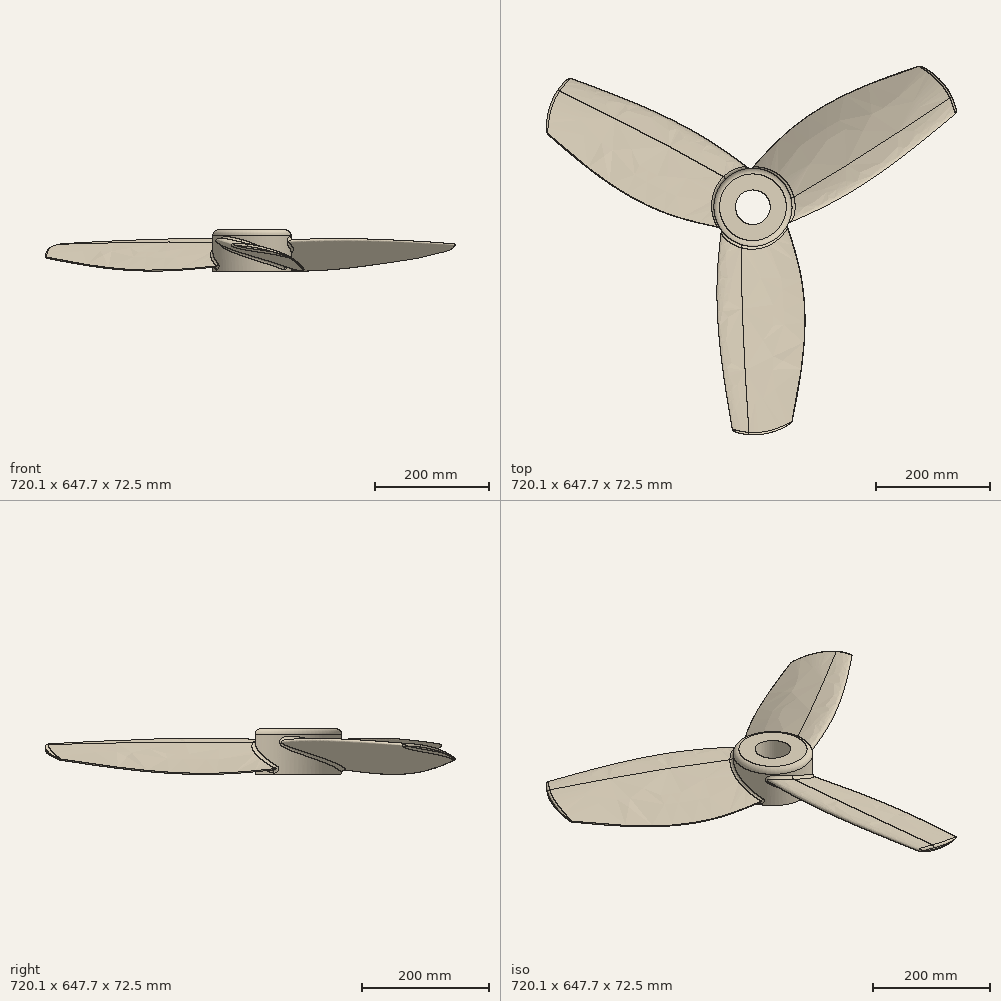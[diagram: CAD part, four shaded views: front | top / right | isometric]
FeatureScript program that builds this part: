
annotation { "Feature Type Name" : "Feature", "Feature Type Description" : "" }
export const myFeature = defineFeature(function(context is Context, id is Id, definition is map)
    precondition{}
    {
        {
            var Q0;
            Q0=qCreatedBy(makeId("Front.planeOp"),FACE);
            var sketch = newSketch(context, id + "F0", { "sketchPlane" : qUnion([Q0])});
            skLineSegment(sketch, "E0", {"start": v(-25.68, 10.16) * mm, "end": v(0, 0) * mm, "construction": true});
            skLineSegment(sketch, "E1", {"start": v(0, 0) * mm, "end": v(25.68, -10.16) * mm, "construction": true});
            skLineSegment(sketch, "E2", {"start": v(25.68, -10.16) * mm, "end": v(51.36, -20.31) * mm, "construction": true});
            skLineSegment(sketch, "E3", {"start": v(51.36, -20.31) * mm, "end": v(77.03, -30.47) * mm, "construction": true});
            skLineSegment(sketch, "E4", {"start": v(0, 0) * mm, "end": v(3.73, 9.44) * mm, "construction": true});
            skLineSegment(sketch, "E5", {"start": v(-25.68, 10.16) * mm, "end": v(-23.81, 14.88) * mm, "construction": true});
            skFitSpline(sketch, "E6", {"points": [v(-25.68, 10.16) * mm, v(3.73, 9.44) * mm, v(77.03, -30.47) * mm], "startDerivative": vector(15.03, 38) * mm, "endDerivative": vector(104.92, -93.69) * mm});
            skPoint(sketch, "E7", {"position": v(1.87, 4.72) * mm});
            skLineSegment(sketch, "E8", {"start": v(-23.81, 14.88) * mm, "end": v(1.87, 4.72) * mm, "construction": true});
            skLineSegment(sketch, "E9", {"start": v(0, 0) * mm, "end": v(-1.87, -4.72) * mm, "construction": true});
            skLineSegment(sketch, "E10", {"start": v(-25.68, 10.16) * mm, "end": v(-27.54, 5.44) * mm, "construction": true});
            skFitSpline(sketch, "E11", {"points": [v(-25.68, 10.16) * mm, v(-1.87, -4.72) * mm, v(77.03, -30.47) * mm], "startDerivative": vector(-15.23, -38.5) * mm, "endDerivative": vector(121.84, -48.19) * mm});
            skLineSegment(sketch, "E12", {"start": v(51.36, -20.31) * mm, "end": v(55.09, -10.87) * mm, "construction": true});
            skSolve(sketch);
        }
        {
            var Q0;
            Q0=qCreatedBy(makeId("Front.planeOp"),FACE);
            cPlane(context, id + "F1", {"entities" : qUnion([Q0]), "cplaneType" : CPlaneType.OFFSET, "offset" : 125 * mm, "width" : 150 * mm, "height" : 150 * mm});
        }
        {
            var Q0;
            Q0=qCreatedBy(id+"F1.planeOp",FACE);
            var sketch = newSketch(context, id + "F2", { "sketchPlane" : qUnion([Q0])});
            skLineSegment(sketch, "E13", {"start": v(-38.33, 14.06) * mm, "end": v(0, 0) * mm, "construction": true});
            skLineSegment(sketch, "E14", {"start": v(0, 0) * mm, "end": v(38.33, -14.06) * mm, "construction": true});
            skLineSegment(sketch, "E15", {"start": v(38.33, -14.06) * mm, "end": v(76.67, -28.12) * mm, "construction": true});
            skLineSegment(sketch, "E16", {"start": v(76.67, -28.12) * mm, "end": v(115, -42.17) * mm, "construction": true});
            skLineSegment(sketch, "E17", {"start": v(0, 0) * mm, "end": v(4.06, 11.06) * mm, "construction": true});
            skLineSegment(sketch, "E18", {"start": v(-38.33, 14.06) * mm, "end": v(-36.3, 19.59) * mm, "construction": true});
            skFitSpline(sketch, "E19", {"points": [v(-38.33, 14.06) * mm, v(4.06, 11.06) * mm, v(115, -42.17) * mm], "startDerivative": vector(16.44, 44.82) * mm, "endDerivative": vector(163.27, -119.63) * mm});
            skPoint(sketch, "E20", {"position": v(2.03, 5.53) * mm});
            skLineSegment(sketch, "E21", {"start": v(-36.3, 19.59) * mm, "end": v(2.03, 5.53) * mm, "construction": true});
            skLineSegment(sketch, "E22", {"start": v(0, 0) * mm, "end": v(-2.03, -5.53) * mm, "construction": true});
            skLineSegment(sketch, "E23", {"start": v(-38.33, 14.06) * mm, "end": v(-40.36, 8.53) * mm, "construction": true});
            skFitSpline(sketch, "E24", {"points": [v(-38.33, 14.06) * mm, v(-2.03, -5.53) * mm, v(115, -42.17) * mm], "startDerivative": vector(-16.57, -45.19) * mm, "endDerivative": vector(181.7, -66.64) * mm});
            skLineSegment(sketch, "E25", {"start": v(76.67, -28.12) * mm, "end": v(80.72, -17.06) * mm, "construction": true});
            skSolve(sketch);
        }
        {
            var Q0;
            Q0=qCreatedBy(makeId("Front.planeOp"),FACE);
            cPlane(context, id + "F3", {"entities" : qUnion([Q0]), "cplaneType" : CPlaneType.OFFSET, "offset" : 400 * mm, "width" : 150 * mm, "height" : 150 * mm});
        }
        {
            var Q0;
            Q0=qCreatedBy(id+"F3.planeOp",FACE);
            var sketch = newSketch(context, id + "F4", { "sketchPlane" : qUnion([Q0])});
            skLineSegment(sketch, "E26", {"start": v(-10.03, 5.14) * mm, "end": v(16.27, 0) * mm, "construction": true});
            skLineSegment(sketch, "E27", {"start": v(16.27, 0) * mm, "end": v(42.56, -5.14) * mm, "construction": true});
            skLineSegment(sketch, "E28", {"start": v(42.56, -5.14) * mm, "end": v(68.86, -10.28) * mm, "construction": true});
            skLineSegment(sketch, "E29", {"start": v(68.86, -10.28) * mm, "end": v(95.16, -15.42) * mm, "construction": true});
            skLineSegment(sketch, "E30", {"start": v(16.27, 0) * mm, "end": v(17.61, 6.9) * mm, "construction": true});
            skLineSegment(sketch, "E31", {"start": v(-10.03, 5.14) * mm, "end": v(-9.36, 8.59) * mm, "construction": true});
            skFitSpline(sketch, "E32", {"points": [v(-10.03, 5.14) * mm, v(17.61, 6.9) * mm, v(95.16, -15.42) * mm], "startDerivative": vector(5.47, 28.01) * mm, "endDerivative": vector(118.7, -57.28) * mm});
            skPoint(sketch, "E33", {"position": v(16.94, 3.45) * mm});
            skLineSegment(sketch, "E34", {"start": v(-9.36, 8.59) * mm, "end": v(16.94, 3.45) * mm, "construction": true});
            skLineSegment(sketch, "E35", {"start": v(16.27, 0) * mm, "end": v(15.6, -3.45) * mm, "construction": true});
            skLineSegment(sketch, "E36", {"start": v(-10.03, 5.14) * mm, "end": v(-10.7, 1.7) * mm, "construction": true});
            skFitSpline(sketch, "E37", {"points": [v(-10.03, 5.14) * mm, v(15.6, -3.45) * mm, v(95.16, -15.42) * mm], "startDerivative": vector(-5.51, -28.2) * mm, "endDerivative": vector(124.61, -24.36) * mm});
            skLineSegment(sketch, "E38", {"start": v(68.86, -10.28) * mm, "end": v(70.2, -3.38) * mm, "construction": true});
            skSolve(sketch);
        }
        {
            var Q0;
            Q0 = qSketchRegion(id + "F0", true);
            var Q1;
            Q1 = qSketchRegion(id + "F2", true);
            var Q2;
            Q2 = qSketchRegion(id + "F4", true);
            var Q3;
            Q3=sQuery(id+"F0.wireOp",VERTEX,"E6.1.internal");
            var Q4;
            Q4=sQuery(id+"F2.wireOp",VERTEX,"E19.1.internal");
            var Q5;
            Q5=sQuery(id+"F4.wireOp",VERTEX,"E30.end");
            loft(context, id + "F5", {"sheetProfilesArray" : [{ "sheetProfileEntities" : qUnion([Q0]) }, { "sheetProfileEntities" : qUnion([Q1]) }, { "sheetProfileEntities" : qUnion([Q2]) }], "matchConnections" : true, "connections" : [{ "connectionEntities" : qUnion([Q3, Q4, Q5]), "connectionEdgeQueries" : qUnion([]), "connectionEdgeParameters" : [] }]});
        }
        {
            var Q0;
            Q0=qCreatedBy(makeId("Top.planeOp"),FACE);
            var sketch = newSketch(context, id + "F6", { "sketchPlane" : qUnion([Q0])});
            skFitSpline(sketch, "E39", {"points": [v(-55.98, -360.47) * mm, v(39.38, -398.87) * mm, v(142.8, -333.19) * mm], "startDerivative": vector(111.22, -150.8) * mm, "endDerivative": vector(54.24, 145.78) * mm});
            skLineSegment(sketch, "E40", {"start": v(-55.98, -360.47) * mm, "end": v(-55.98, -458.75) * mm});
            skLineSegment(sketch, "E41", {"start": v(142.8, -333.19) * mm, "end": v(142.8, -458.75) * mm});
            skLineSegment(sketch, "E42", {"start": v(142.8, -458.75) * mm, "end": v(-55.98, -458.75) * mm});
            skSolve(sketch);
        }
        {
            var Q0;
            Q0 = qSketchRegion(id + "F6", true);
            extrude(context, id + "F7", {"entities" : qUnion([Q0]), "operationType" : NewBodyOperationType.REMOVE, "endBound" : BoundingType.SYMMETRIC, "oppositeDirection" : true, "depth" : 40.17 * mm});
        }
        {
            var Q0;
            Q0=makeQuery(id+"F5.opLoft","SWEPT_EDGE",EDGE,{"disambiguationData":[OSD([sQuery(id+"F2.wireOp",EDGE,"E19"),sQuery(id+"F2.wireOp",EDGE,"E24"),sQuery(id+"F4.wireOp",EDGE,"E32"),sQuery(id+"F4.wireOp",EDGE,"E37")])]});
            fillet(context, id + "F8", {"entities" : qUnion([Q0]), "radius" : 1 * mm, "tangentPropagation" : true, "allowEdgeOverflow" : false});
        }
        {
            var Q0;
            Q0=makeQuery(id+"F7.boolean.opBoolean","COPY",FACE,{"derivedFrom":makeQuery(id+"F7.opExtrude","SWEPT_FACE",FACE,{"disambiguationData":[OSD([sQuery(id+"F6.wireOp",EDGE,"E39")])]})});
            fillet(context, id + "F9", {"entities" : qUnion([Q0]), "radius" : 4 * mm, "tangentPropagation" : true, "allowEdgeOverflow" : false});
        }
        {
            var Q0;
            Q0=qCreatedBy(makeId("Top.planeOp"),FACE);
            var sketch = newSketch(context, id + "F10", { "sketchPlane" : qUnion([Q0])});
            skCircle(sketch, "E43", {"center": v(24.35, 0) * mm, "radius": 68.6 * mm});
            skSolve(sketch);
        }
        {
            var Q0;
            Q0 = qSketchRegion(id + "F10", true);
            extrude(context, id + "F11", {"entities" : qUnion([Q0]), "depth" : 32.31 * mm, "hasSecondDirection" : true, "secondDirectionOppositeDirection" : true, "secondDirectionDepth" : 40 * mm});
        }
        {
            var Q0;
            Q0=makeQuery(id+"F5.opLoft","SWEPT_BODY",BODY,{"disambiguationData":[OSD([makeQuery(id+"F0.imprint","IMPRINT",FACE,{"disambiguationData":[TD([[makeQuery(id+"F0.imprint","IMPRINT",EDGE,{"derivedFrom":sQuery(id+"F0.wireOp",EDGE,"E6")}),-1.0]])]}),sQuery(id+"F2.wireOp",EDGE,"E24"),makeQuery(id+"F4.imprint","IMPRINT",FACE,{"disambiguationData":[TD([[makeQuery(id+"F4.imprint","IMPRINT",EDGE,{"derivedFrom":sQuery(id+"F4.wireOp",EDGE,"E32")}),-1.0]])]})])]});
            var Q1;
            Q1=makeQuery(id+"F11.opExtrude","SWEPT_FACE",FACE,{"disambiguationData":[OSD([sQuery(id+"F10.wireOp",EDGE,"E43")])]});
            circularPattern(context, id + "F12", {"entities" : qUnion([Q0]), "axis" : qUnion([Q1]), "angle" : 360 * degree, "instanceCount" : 3, "equalSpace" : true});
        }
        {
            var Q0;
            Q0=makeQuery(id+"F12.opPattern","COPY",BODY,{"derivedFrom":makeQuery(id+"F5.opLoft","SWEPT_BODY",BODY,{"disambiguationData":[OSD([makeQuery(id+"F0.imprint","IMPRINT",FACE,{"disambiguationData":[TD([[makeQuery(id+"F0.imprint","IMPRINT",EDGE,{"derivedFrom":sQuery(id+"F0.wireOp",EDGE,"E6")}),-1.0]])]}),sQuery(id+"F2.wireOp",EDGE,"E24"),makeQuery(id+"F4.imprint","IMPRINT",FACE,{"disambiguationData":[TD([[makeQuery(id+"F4.imprint","IMPRINT",EDGE,{"derivedFrom":sQuery(id+"F4.wireOp",EDGE,"E32")}),-1.0]])]})])]}),"instanceName":"2"});
            var Q1;
            Q1=makeQuery(id+"F5.opLoft","SWEPT_BODY",BODY,{"disambiguationData":[OSD([makeQuery(id+"F0.imprint","IMPRINT",FACE,{"disambiguationData":[TD([[makeQuery(id+"F0.imprint","IMPRINT",EDGE,{"derivedFrom":sQuery(id+"F0.wireOp",EDGE,"E6")}),-1.0]])]}),sQuery(id+"F2.wireOp",EDGE,"E24"),makeQuery(id+"F4.imprint","IMPRINT",FACE,{"disambiguationData":[TD([[makeQuery(id+"F4.imprint","IMPRINT",EDGE,{"derivedFrom":sQuery(id+"F4.wireOp",EDGE,"E32")}),-1.0]])]})])]});
            var Q2;
            Q2=makeQuery(id+"F11.opExtrude","SWEPT_BODY",BODY,{"disambiguationData":[OSD([sQuery(id+"F10.wireOp",EDGE,"E43")])]});
            var Q3;
            Q3=makeQuery(id+"F12.opPattern","COPY",BODY,{"derivedFrom":makeQuery(id+"F5.opLoft","SWEPT_BODY",BODY,{"disambiguationData":[OSD([makeQuery(id+"F0.imprint","IMPRINT",FACE,{"disambiguationData":[TD([[makeQuery(id+"F0.imprint","IMPRINT",EDGE,{"derivedFrom":sQuery(id+"F0.wireOp",EDGE,"E6")}),-1.0]])]}),sQuery(id+"F2.wireOp",EDGE,"E24"),makeQuery(id+"F4.imprint","IMPRINT",FACE,{"disambiguationData":[TD([[makeQuery(id+"F4.imprint","IMPRINT",EDGE,{"derivedFrom":sQuery(id+"F4.wireOp",EDGE,"E32")}),-1.0]])]})])]}),"instanceName":"1"});
            var Q4;
            Q4=makeQuery(id+"F12.opPattern","COPY",BODY,{"derivedFrom":makeQuery(id+"F5.opLoft","SWEPT_BODY",BODY,{"disambiguationData":[OSD([makeQuery(id+"F0.imprint","IMPRINT",FACE,{"disambiguationData":[TD([[makeQuery(id+"F0.imprint","IMPRINT",EDGE,{"derivedFrom":sQuery(id+"F0.wireOp",EDGE,"E6")}),-1.0]])]}),sQuery(id+"F2.wireOp",EDGE,"E24"),makeQuery(id+"F4.imprint","IMPRINT",FACE,{"disambiguationData":[TD([[makeQuery(id+"F4.imprint","IMPRINT",EDGE,{"derivedFrom":sQuery(id+"F4.wireOp",EDGE,"E32")}),-1.0]])]})])]}),"instanceName":"4"});
            var Q5;
            Q5=makeQuery(id+"F12.opPattern","COPY",BODY,{"derivedFrom":makeQuery(id+"F5.opLoft","SWEPT_BODY",BODY,{"disambiguationData":[OSD([makeQuery(id+"F0.imprint","IMPRINT",FACE,{"disambiguationData":[TD([[makeQuery(id+"F0.imprint","IMPRINT",EDGE,{"derivedFrom":sQuery(id+"F0.wireOp",EDGE,"E6")}),-1.0]])]}),sQuery(id+"F2.wireOp",EDGE,"E24"),makeQuery(id+"F4.imprint","IMPRINT",FACE,{"disambiguationData":[TD([[makeQuery(id+"F4.imprint","IMPRINT",EDGE,{"derivedFrom":sQuery(id+"F4.wireOp",EDGE,"E32")}),-1.0]])]})])]}),"instanceName":"3"});
            booleanBodies(context, id + "F13", {"operationType" : BooleanOperationType.UNION, "tools" : qUnion([Q0, Q1, Q2, Q3, Q4, Q5])});
        }
        {
            var Q0;
            Q0=makeQuery(id+"F11.opExtrude","CAP_FACE",FACE,{"disambiguationData":[OSD([sQuery(id+"F10.wireOp",EDGE,"E43")])],"isStart":false});
            var sketch = newSketch(context, id + "F14", { "sketchPlane" : qUnion([Q0])});
            skCircle(sketch, "E44", {"center": v(24.35, 0) * mm, "radius": 30.45 * mm});
            skSolve(sketch);
        }
        {
            var Q0;
            Q0 = qSketchRegion(id + "F14", true);
            extrude(context, id + "F15", {"entities" : qUnion([Q0]), "operationType" : NewBodyOperationType.REMOVE, "endBound" : BoundingType.THROUGH_ALL, "oppositeDirection" : true, "depth" : 25 * mm});
        }
        {
            var Q0;
            {var subQ0=sQuery(id+"F0.wireOp",VERTEX,"E6.1.internal");var subQ1=sQuery(id+"F0.wireOp",EDGE,"E6");var subQ2=sQuery(id+"F0.wireOp",EDGE,"E11");var subQ3=sQuery(id+"F2.wireOp",VERTEX,"E19.1.internal");var subQ4=sQuery(id+"F2.wireOp",EDGE,"E19");var subQ5=sQuery(id+"F2.wireOp",EDGE,"E24");Q0=makeQuery(id+"F13.opBoolean","INTERSECT",EDGE,{"derivedFrom":[makeQuery(id+"F11.opExtrude","SWEPT_FACE",FACE,{"disambiguationData":[OSD([sQuery(id+"F10.wireOp",EDGE,"E43")])]}),makeQuery(id+"F12.opPattern","COPY",FACE,{"derivedFrom":makeQuery(id+"F5.opLoft","SWEPT_FACE",FACE,{"disambiguationData":[OSD([subQ0,subQ1,subQ2,subQ3,subQ4,subQ5]),TDD([subQ0,makeQuery(id+"F0.imprint","INTERSECT",VERTEX,{"disambiguationData":[OD(0.0)],"derivedFrom":[subQ1,subQ2]}),makeQuery(id+"F0.imprint","IMPRINT",EDGE,{"derivedFrom":subQ1}),subQ3,makeQuery(id+"F2.imprint","INTERSECT",VERTEX,{"disambiguationData":[OD(0.0)],"derivedFrom":[subQ4,subQ5]}),makeQuery(id+"F2.imprint","IMPRINT",EDGE,{"derivedFrom":subQ4})])]}),"instanceName":"2"})]});}
            var Q1;
            {var subQ0=sQuery(id+"F0.wireOp",VERTEX,"E6.1.internal");var subQ1=sQuery(id+"F0.wireOp",EDGE,"E6");var subQ2=sQuery(id+"F0.wireOp",EDGE,"E11");var subQ3=sQuery(id+"F2.wireOp",VERTEX,"E19.1.internal");var subQ4=sQuery(id+"F2.wireOp",EDGE,"E19");var subQ5=sQuery(id+"F2.wireOp",EDGE,"E24");Q1=makeQuery(id+"F13.opBoolean","INTERSECT",EDGE,{"derivedFrom":[makeQuery(id+"F5.opLoft","SWEPT_FACE",FACE,{"disambiguationData":[OSD([subQ0,subQ1,subQ2,subQ3,subQ4,subQ5]),TDD([subQ0,makeQuery(id+"F0.imprint","INTERSECT",VERTEX,{"disambiguationData":[OD(1.0)],"derivedFrom":[subQ1,subQ2]}),makeQuery(id+"F0.imprint","IMPRINT",EDGE,{"derivedFrom":subQ1}),subQ3,makeQuery(id+"F2.imprint","INTERSECT",VERTEX,{"disambiguationData":[OD(1.0)],"derivedFrom":[subQ4,subQ5]}),makeQuery(id+"F2.imprint","IMPRINT",EDGE,{"derivedFrom":subQ4})])]}),makeQuery(id+"F11.opExtrude","SWEPT_FACE",FACE,{"disambiguationData":[OSD([sQuery(id+"F10.wireOp",EDGE,"E43")])]})]});}
            var Q2;
            {var subQ0=sQuery(id+"F0.wireOp",VERTEX,"E6.1.internal");var subQ1=sQuery(id+"F0.wireOp",EDGE,"E6");var subQ2=sQuery(id+"F0.wireOp",EDGE,"E11");var subQ3=sQuery(id+"F2.wireOp",VERTEX,"E19.1.internal");var subQ4=sQuery(id+"F2.wireOp",EDGE,"E19");var subQ5=sQuery(id+"F2.wireOp",EDGE,"E24");Q2=makeQuery(id+"F13.opBoolean","INTERSECT",EDGE,{"derivedFrom":[makeQuery(id+"F11.opExtrude","SWEPT_FACE",FACE,{"disambiguationData":[OSD([sQuery(id+"F10.wireOp",EDGE,"E43")])]}),makeQuery(id+"F12.opPattern","COPY",FACE,{"derivedFrom":makeQuery(id+"F5.opLoft","SWEPT_FACE",FACE,{"disambiguationData":[OSD([subQ0,subQ1,subQ2,subQ3,subQ4,subQ5]),TDD([subQ0,makeQuery(id+"F0.imprint","INTERSECT",VERTEX,{"disambiguationData":[OD(1.0)],"derivedFrom":[subQ1,subQ2]}),makeQuery(id+"F0.imprint","IMPRINT",EDGE,{"derivedFrom":subQ1}),subQ3,makeQuery(id+"F2.imprint","INTERSECT",VERTEX,{"disambiguationData":[OD(1.0)],"derivedFrom":[subQ4,subQ5]}),makeQuery(id+"F2.imprint","IMPRINT",EDGE,{"derivedFrom":subQ4})])]}),"instanceName":"1"})]});}
            var Q3;
            {var subQ0=sQuery(id+"F0.wireOp",VERTEX,"E6.1.internal");var subQ1=sQuery(id+"F0.wireOp",EDGE,"E6");var subQ2=sQuery(id+"F0.wireOp",EDGE,"E11");var subQ3=sQuery(id+"F2.wireOp",VERTEX,"E19.1.internal");var subQ4=sQuery(id+"F2.wireOp",EDGE,"E19");var subQ5=sQuery(id+"F2.wireOp",EDGE,"E24");Q3=makeQuery(id+"F13.opBoolean","INTERSECT",EDGE,{"derivedFrom":[makeQuery(id+"F11.opExtrude","SWEPT_FACE",FACE,{"disambiguationData":[OSD([sQuery(id+"F10.wireOp",EDGE,"E43")])]}),makeQuery(id+"F12.opPattern","COPY",FACE,{"derivedFrom":makeQuery(id+"F5.opLoft","SWEPT_FACE",FACE,{"disambiguationData":[OSD([subQ0,subQ1,subQ2,subQ3,subQ4,subQ5]),TDD([subQ0,makeQuery(id+"F0.imprint","INTERSECT",VERTEX,{"disambiguationData":[OD(1.0)],"derivedFrom":[subQ1,subQ2]}),makeQuery(id+"F0.imprint","IMPRINT",EDGE,{"derivedFrom":subQ1}),subQ3,makeQuery(id+"F2.imprint","INTERSECT",VERTEX,{"disambiguationData":[OD(1.0)],"derivedFrom":[subQ4,subQ5]}),makeQuery(id+"F2.imprint","IMPRINT",EDGE,{"derivedFrom":subQ4})])]}),"instanceName":"4"})]});}
            var Q4;
            {var subQ0=sQuery(id+"F0.wireOp",VERTEX,"E6.1.internal");var subQ1=sQuery(id+"F0.wireOp",EDGE,"E6");var subQ2=sQuery(id+"F0.wireOp",EDGE,"E11");var subQ3=sQuery(id+"F2.wireOp",VERTEX,"E19.1.internal");var subQ4=sQuery(id+"F2.wireOp",EDGE,"E19");var subQ5=sQuery(id+"F2.wireOp",EDGE,"E24");Q4=makeQuery(id+"F13.opBoolean","INTERSECT",EDGE,{"derivedFrom":[makeQuery(id+"F11.opExtrude","SWEPT_FACE",FACE,{"disambiguationData":[OSD([sQuery(id+"F10.wireOp",EDGE,"E43")])]}),makeQuery(id+"F12.opPattern","COPY",FACE,{"derivedFrom":makeQuery(id+"F5.opLoft","SWEPT_FACE",FACE,{"disambiguationData":[OSD([subQ0,subQ1,subQ2,subQ3,subQ4,subQ5]),TDD([subQ0,makeQuery(id+"F0.imprint","INTERSECT",VERTEX,{"disambiguationData":[OD(0.0)],"derivedFrom":[subQ1,subQ2]}),makeQuery(id+"F0.imprint","IMPRINT",EDGE,{"derivedFrom":subQ1}),subQ3,makeQuery(id+"F2.imprint","INTERSECT",VERTEX,{"disambiguationData":[OD(0.0)],"derivedFrom":[subQ4,subQ5]}),makeQuery(id+"F2.imprint","IMPRINT",EDGE,{"derivedFrom":subQ4})])]}),"instanceName":"3"})]});}
            fillet(context, id + "F16", {"entities" : qUnion([Q0, Q1, Q2, Q3, Q4]), "radius" : 5 * mm, "tangentPropagation" : true, "allowEdgeOverflow" : false});
        }
        {
            var Q0;
            Q0=makeQuery(id+"F11.opExtrude","CAP_EDGE",EDGE,{"disambiguationData":[OSD([sQuery(id+"F10.wireOp",EDGE,"E43")])],"isStart":false});
            fillet(context, id + "F17", {"entities" : qUnion([Q0]), "radius" : 10 * mm, "tangentPropagation" : true, "allowEdgeOverflow" : false});
        }
    });
